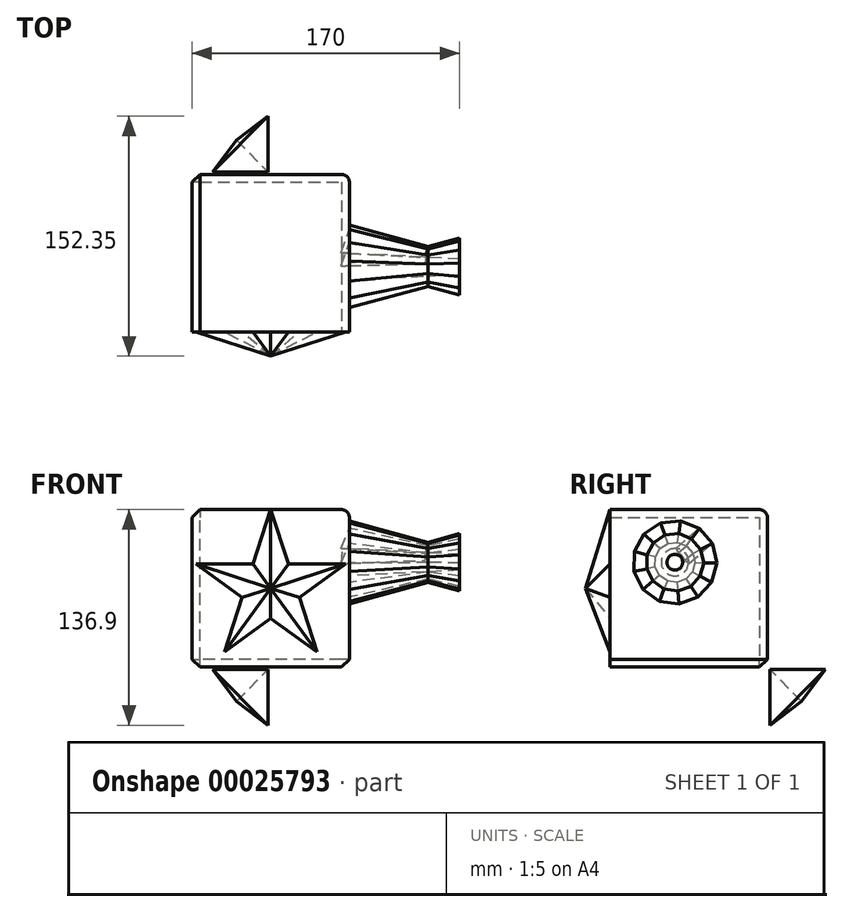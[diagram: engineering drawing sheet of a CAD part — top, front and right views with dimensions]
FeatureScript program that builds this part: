
annotation { "Feature Type Name" : "Feature", "Feature Type Description" : "" }
export const myFeature = defineFeature(function(context is Context, id is Id, definition is map)
    precondition{}
    {
        {
            var Q0;
            Q0=qCreatedBy(makeId("Top.planeOp"),FACE);
            var sketch = newSketch(context, id + "F0", { "sketchPlane" : qUnion([Q0])});
            skLineSegment(sketch, "E0.rect.bottom", {"start": v(50, -50) * mm, "end": v(-50, -50) * mm});
            skLineSegment(sketch, "E0.rect.top", {"start": v(50, 50) * mm, "end": v(-50, 50) * mm});
            skLineSegment(sketch, "E0.rect.left", {"start": v(50, -50) * mm, "end": v(50, 50) * mm});
            skLineSegment(sketch, "E0.rect.right", {"start": v(-50, -50) * mm, "end": v(-50, 50) * mm});
            skPoint(sketch, "E0.rect.middle", {"position": v(0, 0) * mm});
            skSolve(sketch);
        }
        {
            var Q0;
            Q0=makeQuery(id+"F0.imprint","IMPRINT",FACE,{"disambiguationData":[TD([[makeQuery(id+"F0.imprint","IMPRINT",EDGE,{"derivedFrom":sQuery(id+"F0.wireOp",EDGE,"E0.rect.bottom")}),-1.0]])]});
            extrude(context, id + "F1", {"entities" : qUnion([Q0]), "depth" : 100 * mm});
        }
        {
            var Q0;
            Q0=makeQuery(id+"F1.opExtrude","SWEPT_FACE",FACE,{"disambiguationData":[OSD([sQuery(id+"F0.wireOp",EDGE,"E0.rect.left")])]});
            var sketch = newSketch(context, id + "F2", { "sketchPlane" : qUnion([Q0])});
            skCircle(sketch, "E1.cCircle", {"center": v(-8.75, 66.58) * mm, "radius": 25.84 * mm, "construction": true});
            skLineSegment(sketch, "E1.0", {"start": v(17.86, 66.11) * mm, "end": v(14.6, 53.8) * mm});
            skLineSegment(sketch, "E1.1", {"start": v(14.6, 53.8) * mm, "end": v(5.98, 44.41) * mm});
            skLineSegment(sketch, "E1.2", {"start": v(5.98, 44.41) * mm, "end": v(-6, 40.1) * mm});
            skLineSegment(sketch, "E1.3", {"start": v(-6, 40.1) * mm, "end": v(-18.62, 41.86) * mm});
            skLineSegment(sketch, "E1.4", {"start": v(-18.62, 41.86) * mm, "end": v(-28.98, 49.28) * mm});
            skLineSegment(sketch, "E1.5", {"start": v(-28.98, 49.28) * mm, "end": v(-34.7, 60.66) * mm});
            skLineSegment(sketch, "E1.6", {"start": v(-34.7, 60.66) * mm, "end": v(-34.48, 73.4) * mm});
            skLineSegment(sketch, "E1.7", {"start": v(-34.48, 73.4) * mm, "end": v(-28.37, 84.57) * mm});
            skLineSegment(sketch, "E1.8", {"start": v(-28.37, 84.57) * mm, "end": v(-17.76, 91.62) * mm});
            skLineSegment(sketch, "E1.9", {"start": v(-17.76, 91.62) * mm, "end": v(-5.09, 92.94) * mm});
            skLineSegment(sketch, "E1.10", {"start": v(-5.09, 92.94) * mm, "end": v(6.74, 88.21) * mm});
            skLineSegment(sketch, "E1.11", {"start": v(6.74, 88.21) * mm, "end": v(15.02, 78.53) * mm});
            skLineSegment(sketch, "E1.12", {"start": v(15.02, 78.53) * mm, "end": v(17.86, 66.11) * mm});
            skPoint(sketch, "E1.0.midPoint", {"position": v(16.23, 59.96) * mm});
            skSolve(sketch);
        }
        {
            var Q0;
            Q0=makeQuery(id+"F2.imprint","IMPRINT",FACE,{"disambiguationData":[TD([[makeQuery(id+"F2.imprint","IMPRINT",EDGE,{"derivedFrom":sQuery(id+"F2.wireOp",EDGE,"E1.0")}),-1.0]])]});
            extrude(context, id + "F3", {"entities" : qUnion([Q0]), "operationType" : NewBodyOperationType.ADD, "depth" : 50 * mm, "hasDraft" : true, "draftAngle" : 15 * degree, "draftPullDirection" : true});
        }
        {
            var Q0;
            Q0=makeQuery(id+"F3.opExtrude","CAP_FACE",FACE,{"disambiguationData":[OSD([sQuery(id+"F2.wireOp",EDGE,"E1.0"),sQuery(id+"F2.wireOp",EDGE,"E1.1"),sQuery(id+"F2.wireOp",EDGE,"E1.2"),sQuery(id+"F2.wireOp",EDGE,"E1.3"),sQuery(id+"F2.wireOp",EDGE,"E1.4"),sQuery(id+"F2.wireOp",EDGE,"E1.5"),sQuery(id+"F2.wireOp",EDGE,"E1.6"),sQuery(id+"F2.wireOp",EDGE,"E1.7"),sQuery(id+"F2.wireOp",EDGE,"E1.8"),sQuery(id+"F2.wireOp",EDGE,"E1.9"),sQuery(id+"F2.wireOp",EDGE,"E1.10"),sQuery(id+"F2.wireOp",EDGE,"E1.11"),sQuery(id+"F2.wireOp",EDGE,"E1.12")])],"isStart":false});
            var sketch = newSketch(context, id + "F4", { "sketchPlane" : qUnion([Q0])});
            skLineSegment(sketch, "E2", {"start": v(-6.99, 79.27) * mm, "end": v(-1.3, 77) * mm});
            skLineSegment(sketch, "E3", {"start": v(-1.3, 77) * mm, "end": v(2.7, 72.33) * mm});
            skLineSegment(sketch, "E4", {"start": v(2.7, 72.33) * mm, "end": v(4.06, 66.35) * mm});
            skLineSegment(sketch, "E5", {"start": v(4.06, 66.35) * mm, "end": v(2.49, 60.42) * mm});
            skLineSegment(sketch, "E6", {"start": v(2.49, 60.42) * mm, "end": v(-1.66, 55.9) * mm});
            skLineSegment(sketch, "E7", {"start": v(-1.66, 55.9) * mm, "end": v(-7.43, 53.83) * mm});
            skLineSegment(sketch, "E8", {"start": v(-7.43, 53.83) * mm, "end": v(-13.5, 54.67) * mm});
            skLineSegment(sketch, "E9", {"start": v(-13.5, 54.67) * mm, "end": v(-18.5, 58.25) * mm});
            skLineSegment(sketch, "E10", {"start": v(-18.5, 58.25) * mm, "end": v(-21.25, 63.73) * mm});
            skLineSegment(sketch, "E11", {"start": v(-21.25, 63.73) * mm, "end": v(-21.14, 69.86) * mm});
            skLineSegment(sketch, "E12", {"start": v(-21.14, 69.86) * mm, "end": v(-18.2, 75.24) * mm});
            skLineSegment(sketch, "E13", {"start": v(-18.2, 75.24) * mm, "end": v(-13.1, 78.64) * mm});
            skLineSegment(sketch, "E14", {"start": v(-13.1, 78.64) * mm, "end": v(-6.99, 79.27) * mm});
            skSolve(sketch);
        }
        {
            var Q0;
            Q0 = qSketchRegion(id + "F4", true);
            extrude(context, id + "F5", {"entities" : qUnion([Q0]), "operationType" : NewBodyOperationType.ADD, "depth" : 20 * mm, "hasDraft" : true, "draftAngle" : 15 * degree});
        }
        {
            var Q0;
            Q0=makeQuery(id+"F5.opExtrude","CAP_FACE",FACE,{"disambiguationData":[OSD([sQuery(id+"F4.wireOp",EDGE,"E2"),sQuery(id+"F4.wireOp",EDGE,"E3"),sQuery(id+"F4.wireOp",EDGE,"E4"),sQuery(id+"F4.wireOp",EDGE,"E5"),sQuery(id+"F4.wireOp",EDGE,"E6"),sQuery(id+"F4.wireOp",EDGE,"E7"),sQuery(id+"F4.wireOp",EDGE,"E8"),sQuery(id+"F4.wireOp",EDGE,"E9"),sQuery(id+"F4.wireOp",EDGE,"E10"),sQuery(id+"F4.wireOp",EDGE,"E11"),sQuery(id+"F4.wireOp",EDGE,"E12"),sQuery(id+"F4.wireOp",EDGE,"E13"),sQuery(id+"F4.wireOp",EDGE,"E14")])],"isStart":false});
            var sketch = newSketch(context, id + "F6", { "sketchPlane" : qUnion([Q0])});
            skLineSegment(sketch, "E15", {"start": v(-26.63, 62.5) * mm, "end": v(8.6, 70.54) * mm});
            skLineSegment(sketch, "E16", {"start": v(8.6, 70.54) * mm, "end": v(-14.96, 83.83) * mm});
            skLineSegment(sketch, "E17", {"start": v(-14.96, 83.83) * mm, "end": v(-2.73, 49.82) * mm});
            skLineSegment(sketch, "E18", {"start": v(-2.73, 49.82) * mm, "end": v(-26.48, 71.27) * mm});
            skLineSegment(sketch, "E19", {"start": v(-26.48, 71.27) * mm, "end": v(8.46, 62.02) * mm});
            skCircle(sketch, "E20", {"center": v(-8.75, 66.58) * mm, "radius": 5 * mm});
            skSolve(sketch);
        }
        {
            var Q0;
            {var subQ1=sQuery(id+"F6.wireOp",EDGE,"E15");var subQ3=sQuery(id+"F6.wireOp",EDGE,"E20");var subQ5=makeQuery(id+"F6.imprint","INTERSECT",VERTEX,{"disambiguationData":[OD(0.0)],"derivedFrom":[subQ1,subQ3]});Q0=makeQuery(id+"F6.imprint","IMPRINT",FACE,{"disambiguationData":[TD([[makeQuery(id+"F6.imprint","IMPRINT",EDGE,{"disambiguationData":[TD([[subQ5,-1.0]])],"derivedFrom":subQ3}),1.0]])]});}
            var Q1;
            {var subQ0=sQuery(id+"F6.wireOp",EDGE,"E20");var subQ3=sQuery(id+"F6.wireOp",EDGE,"E15");var subQ4=makeQuery(id+"F6.imprint","INTERSECT",VERTEX,{"disambiguationData":[OD(0.0)],"derivedFrom":[subQ3,subQ0]});Q1=makeQuery(id+"F6.imprint","IMPRINT",FACE,{"disambiguationData":[TD([[makeQuery(id+"F6.imprint","IMPRINT",EDGE,{"disambiguationData":[TD([[subQ4,1.0]])],"derivedFrom":subQ0}),1.0]])]});}
            var Q2;
            {var subQ0=sQuery(id+"F6.wireOp",EDGE,"E20");var subQ3=sQuery(id+"F6.wireOp",EDGE,"E17");var subQ4=makeQuery(id+"F6.imprint","INTERSECT",VERTEX,{"disambiguationData":[OD(0.0)],"derivedFrom":[subQ3,subQ0]});Q2=makeQuery(id+"F6.imprint","IMPRINT",FACE,{"disambiguationData":[TD([[makeQuery(id+"F6.imprint","IMPRINT",EDGE,{"disambiguationData":[TD([[subQ4,-1.0]])],"derivedFrom":subQ0}),1.0]])]});}
            var Q3;
            {var subQ0=sQuery(id+"F6.wireOp",EDGE,"E20");var subQ3=sQuery(id+"F6.wireOp",EDGE,"E15");var subQ4=makeQuery(id+"F6.imprint","INTERSECT",VERTEX,{"disambiguationData":[OD(1.0)],"derivedFrom":[subQ3,subQ0]});Q3=makeQuery(id+"F6.imprint","IMPRINT",FACE,{"disambiguationData":[TD([[makeQuery(id+"F6.imprint","IMPRINT",EDGE,{"disambiguationData":[TD([[subQ4,-1.0]])],"derivedFrom":subQ0}),1.0]])]});}
            var Q4;
            {var subQ0=sQuery(id+"F6.wireOp",EDGE,"E20");var subQ3=sQuery(id+"F6.wireOp",EDGE,"E15");var subQ4=makeQuery(id+"F6.imprint","INTERSECT",VERTEX,{"disambiguationData":[OD(1.0)],"derivedFrom":[subQ3,subQ0]});Q4=makeQuery(id+"F6.imprint","IMPRINT",FACE,{"disambiguationData":[TD([[makeQuery(id+"F6.imprint","IMPRINT",EDGE,{"disambiguationData":[TD([[subQ4,1.0]])],"derivedFrom":subQ0}),1.0]])]});}
            var Q5;
            {var subQ0=sQuery(id+"F6.wireOp",EDGE,"E20");var subQ3=sQuery(id+"F6.wireOp",EDGE,"E17");var subQ4=makeQuery(id+"F6.imprint","INTERSECT",VERTEX,{"disambiguationData":[OD(1.0)],"derivedFrom":[subQ3,subQ0]});Q5=makeQuery(id+"F6.imprint","IMPRINT",FACE,{"disambiguationData":[TD([[makeQuery(id+"F6.imprint","IMPRINT",EDGE,{"disambiguationData":[TD([[subQ4,-1.0]])],"derivedFrom":subQ0}),1.0]])]});}
            var Q6;
            Q6=makeQuery(id+"F1.opExtrude","SWEPT_FACE",FACE,{"disambiguationData":[OSD([sQuery(id+"F0.wireOp",EDGE,"E0.rect.left")])]});
            extrude(context, id + "F7", {"entities" : qUnion([Q0, Q1, Q2, Q3, Q4, Q5]), "operationType" : NewBodyOperationType.REMOVE, "endBound" : BoundingType.UP_TO_SURFACE, "oppositeDirection" : true, "endBoundEntityFace" : qUnion([Q6]), "depth" : 70 * mm, "hasDraft" : true, "draftAngle" : 3 * degree});
        }
        {
            var Q0;
            Q0=makeQuery(id+"F3.opExtrude","SWEPT_FACE",FACE,{"disambiguationData":[OSD([sQuery(id+"F2.wireOp",EDGE,"E1.11")])]});
            var sketch = newSketch(context, id + "F8", { "sketchPlane" : qUnion([Q0])});
            skLineSegment(sketch, "E21", {"start": v(-32.13, 62.65) * mm, "end": v(-32.13, 49.92) * mm});
            skLineSegment(sketch, "E22", {"start": v(-32.13, 49.92) * mm, "end": v(-83.9, 53.22) * mm});
            skLineSegment(sketch, "E23", {"start": v(-83.9, 53.22) * mm, "end": v(-83.9, 59.35) * mm});
            skLineSegment(sketch, "E24", {"start": v(-83.9, 59.35) * mm, "end": v(-32.13, 62.65) * mm});
            skSolve(sketch);
        }
        {
            var Q0;
            Q0 = qSketchRegion(id + "F8", true);
            var Q1;
            Q1=makeQuery(id+"F7.boolean.opBoolean","COPY",FACE,{"derivedFrom":makeQuery(id+"F7.opExtrude","SWEPT_FACE",FACE,{"disambiguationData":[OSD([sQuery(id+"F6.wireOp",EDGE,"E20")])]})});
            extrude(context, id + "F9", {"entities" : qUnion([Q0]), "operationType" : NewBodyOperationType.REMOVE, "endBound" : BoundingType.UP_TO_SURFACE, "oppositeDirection" : true, "endBoundEntityFace" : qUnion([Q1]), "depth" : 25 * mm});
        }
        {
            var Q0;
            Q0=makeQuery(id+"F1.opExtrude","CAP_EDGE",EDGE,{"disambiguationData":[OSD([sQuery(id+"F0.wireOp",EDGE,"E0.rect.top")])],"isStart":false});
            var Q1;
            Q1=makeQuery(id+"F1.opExtrude","CAP_EDGE",EDGE,{"disambiguationData":[OSD([sQuery(id+"F0.wireOp",EDGE,"E0.rect.left")])],"isStart":false});
            var Q2;
            Q2=makeQuery(id+"F1.opExtrude","SWEPT_EDGE",EDGE,{"disambiguationData":[OSD([sQuery(id+"F0.wireOp",EDGE,"E0.rect.top"),sQuery(id+"F0.wireOp",EDGE,"E0.rect.left")])]});
            fillet(context, id + "F10", {"entities" : qUnion([Q0, Q1, Q2]), "radius" : 5 * mm, "tangentPropagation" : true, "allowEdgeOverflow" : false});
        }
        {
            var Q0;
            Q0=makeQuery(id+"F1.opExtrude","SWEPT_EDGE",EDGE,{"disambiguationData":[OSD([sQuery(id+"F0.wireOp",EDGE,"E0.rect.top"),sQuery(id+"F0.wireOp",EDGE,"E0.rect.right")])]});
            var Q1;
            Q1=makeQuery(id+"F1.opExtrude","CAP_EDGE",EDGE,{"disambiguationData":[OSD([sQuery(id+"F0.wireOp",EDGE,"E0.rect.top")])],"isStart":true});
            var Q2;
            Q2=makeQuery(id+"F1.opExtrude","CAP_EDGE",EDGE,{"disambiguationData":[OSD([sQuery(id+"F0.wireOp",EDGE,"E0.rect.right")])],"isStart":true});
            chamfer(context, id + "F11", {"entities" : qUnion([Q0, Q1, Q2]), "width" : 5 * mm, "tangentPropagation" : true});
        }
        {
            var Q0;
            {var subQ0=sQuery(id+"F0.wireOp",EDGE,"E0.rect.top");var subQ1=sQuery(id+"F0.wireOp",EDGE,"E0.rect.right");Q0=makeQuery(id+"F11.opChamfer","BLEND_FACE",FACE,{"disambiguationData":[OSD([subQ0,subQ1]),TDD([makeQuery(id+"F1.opExtrude","CAP_VERTEX",VERTEX,{"disambiguationData":[OSD([subQ0,subQ1])],"isStart":true})])]});}
            var sketch = newSketch(context, id + "F12", { "sketchPlane" : qUnion([Q0])});
            skLineSegment(sketch, "E25", {"start": v(-34.85, 10.36) * mm, "end": v(8.46, 35.36) * mm});
            skLineSegment(sketch, "E26", {"start": v(8.46, 35.36) * mm, "end": v(-34.85, 60.36) * mm});
            skLineSegment(sketch, "E27", {"start": v(-34.85, 60.36) * mm, "end": v(-34.85, 10.36) * mm});
            skLineSegment(sketch, "E28", {"start": v(-34.85, 60.36) * mm, "end": v(-13.2, 22.86) * mm});
            skLineSegment(sketch, "E29", {"start": v(-34.85, 10.36) * mm, "end": v(-13.2, 47.86) * mm});
            skLineSegment(sketch, "E30", {"start": v(8.46, 35.36) * mm, "end": v(-34.85, 35.36) * mm});
            skSolve(sketch);
        }
        {
            var Q0;
            Q0 = qSketchRegion(id + "F12", true);
            extrude(context, id + "F13", {"entities" : qUnion([Q0]), "operationType" : NewBodyOperationType.ADD, "depth" : 25 * mm, "hasDraft" : true, "draftAngle" : 45 * degree, "draftPullDirection" : true});
        }
        {
            var Q0;
            Q0=makeQuery(id+"F1.opExtrude","SWEPT_FACE",FACE,{"disambiguationData":[OSD([sQuery(id+"F0.wireOp",EDGE,"E0.rect.bottom")])]});
            var sketch = newSketch(context, id + "F14", { "sketchPlane" : qUnion([Q0])});
            skLineSegment(sketch, "E31", {"start": v(47.5, 2.5) * mm, "end": v(-47.5, 97.5) * mm});
            skLineSegment(sketch, "E32", {"start": v(-47.5, 97.5) * mm, "end": v(-47.5, 2.5) * mm});
            skLineSegment(sketch, "E33", {"start": v(-47.5, 2.5) * mm, "end": v(48.54, 98.54) * mm});
            skLineSegment(sketch, "E34", {"start": v(0, 50) * mm, "end": v(0, 100) * mm});
            skLineSegment(sketch, "E35", {"start": v(0, 50) * mm, "end": v(-47.55, 65.45) * mm});
            skLineSegment(sketch, "E36", {"start": v(0, 50) * mm, "end": v(47.55, 65.45) * mm});
            skLineSegment(sketch, "E37", {"start": v(0, 50) * mm, "end": v(-29.39, 9.55) * mm});
            skLineSegment(sketch, "E38", {"start": v(0, 50) * mm, "end": v(29.39, 9.55) * mm});
            skLineSegment(sketch, "E39", {"start": v(-47.55, 65.45) * mm, "end": v(47.55, 65.45) * mm});
            skLineSegment(sketch, "E40", {"start": v(47.55, 65.45) * mm, "end": v(-29.39, 9.55) * mm});
            skLineSegment(sketch, "E41", {"start": v(-29.39, 9.55) * mm, "end": v(0, 100) * mm});
            skLineSegment(sketch, "E42", {"start": v(0, 100) * mm, "end": v(29.39, 9.55) * mm});
            skLineSegment(sketch, "E43", {"start": v(29.39, 9.55) * mm, "end": v(-47.55, 65.45) * mm});
            skSolve(sketch);
        }
        {
            var Q0;
            {var subQ0=sQuery(id+"F14.wireOp",EDGE,"E42");var subQ3=sQuery(id+"F14.wireOp",EDGE,"E31");var subQ4=makeQuery(id+"F14.imprint","INTERSECT",VERTEX,{"derivedFrom":[subQ3,subQ0]});Q0=makeQuery(id+"F14.imprint","IMPRINT",FACE,{"disambiguationData":[TD([[makeQuery(id+"F14.imprint","IMPRINT",EDGE,{"disambiguationData":[TD([[subQ4,-1.0]])],"derivedFrom":subQ3}),-1.0]])]});}
            var Q1;
            {var subQ0=sQuery(id+"F14.wireOp",EDGE,"E41");var subQ3=sQuery(id+"F14.wireOp",EDGE,"E31");var subQ4=makeQuery(id+"F14.imprint","INTERSECT",VERTEX,{"derivedFrom":[subQ3,subQ0]});Q1=makeQuery(id+"F14.imprint","IMPRINT",FACE,{"disambiguationData":[TD([[makeQuery(id+"F14.imprint","IMPRINT",EDGE,{"disambiguationData":[TD([[subQ4,-1.0]])],"derivedFrom":subQ3}),-1.0]])]});}
            var Q2;
            {var subQ0=sQuery(id+"F14.wireOp",EDGE,"E39");var subQ1=sQuery(id+"F14.wireOp",EDGE,"E32");var subQ2=makeQuery(id+"F14.imprint","INTERSECT",VERTEX,{"derivedFrom":[subQ1,subQ0]});Q2=makeQuery(id+"F14.imprint","IMPRINT",FACE,{"disambiguationData":[TD([[makeQuery(id+"F14.imprint","IMPRINT",EDGE,{"disambiguationData":[TD([[subQ2,-1.0]])],"derivedFrom":subQ1}),-1.0]])]});}
            var Q3;
            {var subQ1=sQuery(id+"F14.wireOp",EDGE,"E32");var subQ3=sQuery(id+"F14.wireOp",EDGE,"E35");var subQ5=makeQuery(id+"F14.imprint","INTERSECT",VERTEX,{"derivedFrom":[subQ1,subQ3]});Q3=makeQuery(id+"F14.imprint","IMPRINT",FACE,{"disambiguationData":[TD([[makeQuery(id+"F14.imprint","IMPRINT",EDGE,{"disambiguationData":[TD([[subQ5,-1.0]])],"derivedFrom":subQ1}),-1.0]])]});}
            var Q4;
            {var subQ0=sQuery(id+"F14.wireOp",EDGE,"E42");var subQ3=sQuery(id+"F14.wireOp",EDGE,"E33");var subQ4=makeQuery(id+"F14.imprint","INTERSECT",VERTEX,{"derivedFrom":[subQ3,subQ0]});Q4=makeQuery(id+"F14.imprint","IMPRINT",FACE,{"disambiguationData":[TD([[makeQuery(id+"F14.imprint","IMPRINT",EDGE,{"disambiguationData":[TD([[subQ4,-1.0]])],"derivedFrom":subQ3}),1.0]])]});}
            var Q5;
            {var subQ0=sQuery(id+"F14.wireOp",EDGE,"E42");var subQ3=sQuery(id+"F14.wireOp",EDGE,"E36");var subQ4=makeQuery(id+"F14.imprint","INTERSECT",VERTEX,{"derivedFrom":[subQ3,subQ0]});Q5=makeQuery(id+"F14.imprint","IMPRINT",FACE,{"disambiguationData":[TD([[makeQuery(id+"F14.imprint","IMPRINT",EDGE,{"disambiguationData":[TD([[subQ4,-1.0]])],"derivedFrom":subQ0}),1.0]])]});}
            var Q6;
            {var subQ0=sQuery(id+"F14.wireOp",EDGE,"E43");var subQ3=sQuery(id+"F14.wireOp",EDGE,"E37");var subQ4=makeQuery(id+"F14.imprint","INTERSECT",VERTEX,{"derivedFrom":[subQ3,subQ0]});Q6=makeQuery(id+"F14.imprint","IMPRINT",FACE,{"disambiguationData":[TD([[makeQuery(id+"F14.imprint","IMPRINT",EDGE,{"disambiguationData":[TD([[subQ4,1.0]])],"derivedFrom":subQ0}),1.0]])]});}
            var Q7;
            {var subQ1=sQuery(id+"F14.wireOp",EDGE,"E40");var subQ3=sQuery(id+"F14.wireOp",EDGE,"E38");var subQ5=makeQuery(id+"F14.imprint","INTERSECT",VERTEX,{"derivedFrom":[subQ3,subQ1]});Q7=makeQuery(id+"F14.imprint","IMPRINT",FACE,{"disambiguationData":[TD([[makeQuery(id+"F14.imprint","IMPRINT",EDGE,{"disambiguationData":[TD([[subQ5,-1.0]])],"derivedFrom":subQ1}),1.0]])]});}
            var Q8;
            {var subQ0=sQuery(id+"F14.wireOp",EDGE,"E42");var subQ1=sQuery(id+"F14.wireOp",EDGE,"E31");var subQ2=makeQuery(id+"F14.imprint","INTERSECT",VERTEX,{"derivedFrom":[subQ1,subQ0]});Q8=makeQuery(id+"F14.imprint","IMPRINT",FACE,{"disambiguationData":[TD([[makeQuery(id+"F14.imprint","IMPRINT",EDGE,{"disambiguationData":[TD([[subQ2,-1.0]])],"derivedFrom":subQ1}),1.0]])]});}
            var Q9;
            {var subQ1=sQuery(id+"F14.wireOp",EDGE,"E40");var subQ5=sQuery(id+"F14.wireOp",EDGE,"E31");var subQ6=makeQuery(id+"F14.imprint","INTERSECT",VERTEX,{"derivedFrom":[subQ5,subQ1]});Q9=makeQuery(id+"F14.imprint","IMPRINT",FACE,{"disambiguationData":[TD([[makeQuery(id+"F14.imprint","IMPRINT",EDGE,{"disambiguationData":[TD([[subQ6,1.0]])],"derivedFrom":subQ1}),-1.0]])]});}
            var Q10;
            {var subQ3=sQuery(id+"F14.wireOp",EDGE,"E33");var subQ5=sQuery(id+"F14.wireOp",EDGE,"E41");var subQ6=makeQuery(id+"F14.imprint","INTERSECT",VERTEX,{"derivedFrom":[subQ3,subQ5]});Q10=makeQuery(id+"F14.imprint","IMPRINT",FACE,{"disambiguationData":[TD([[makeQuery(id+"F14.imprint","IMPRINT",EDGE,{"disambiguationData":[TD([[subQ6,-1.0]])],"derivedFrom":subQ3}),-1.0]])]});}
            var Q11;
            {var subQ0=sQuery(id+"F14.wireOp",EDGE,"E42");var subQ3=sQuery(id+"F14.wireOp",EDGE,"E33");var subQ4=makeQuery(id+"F14.imprint","INTERSECT",VERTEX,{"derivedFrom":[subQ3,subQ0]});Q11=makeQuery(id+"F14.imprint","IMPRINT",FACE,{"disambiguationData":[TD([[makeQuery(id+"F14.imprint","IMPRINT",EDGE,{"disambiguationData":[TD([[subQ4,-1.0]])],"derivedFrom":subQ3}),-1.0]])]});}
            var Q12;
            {var subQ0=sQuery(id+"F14.wireOp",EDGE,"E41");var subQ3=sQuery(id+"F14.wireOp",EDGE,"E31");var subQ4=makeQuery(id+"F14.imprint","INTERSECT",VERTEX,{"derivedFrom":[subQ3,subQ0]});Q12=makeQuery(id+"F14.imprint","IMPRINT",FACE,{"disambiguationData":[TD([[makeQuery(id+"F14.imprint","IMPRINT",EDGE,{"disambiguationData":[TD([[subQ4,1.0]])],"derivedFrom":subQ0}),-1.0]])]});}
            var Q13;
            {var subQ0=sQuery(id+"F14.wireOp",EDGE,"E41");var subQ3=sQuery(id+"F14.wireOp",EDGE,"E31");var subQ4=makeQuery(id+"F14.imprint","INTERSECT",VERTEX,{"derivedFrom":[subQ3,subQ0]});Q13=makeQuery(id+"F14.imprint","IMPRINT",FACE,{"disambiguationData":[TD([[makeQuery(id+"F14.imprint","IMPRINT",EDGE,{"disambiguationData":[TD([[subQ4,-1.0]])],"derivedFrom":subQ3}),1.0]])]});}
            var Q14;
            {var subQ3=sQuery(id+"F14.wireOp",EDGE,"E32");var subQ5=sQuery(id+"F14.wireOp",EDGE,"E35");var subQ7=makeQuery(id+"F14.imprint","INTERSECT",VERTEX,{"derivedFrom":[subQ3,subQ5]});Q14=makeQuery(id+"F14.imprint","IMPRINT",FACE,{"disambiguationData":[TD([[makeQuery(id+"F14.imprint","IMPRINT",EDGE,{"disambiguationData":[TD([[subQ7,-1.0]])],"derivedFrom":subQ3}),1.0]])]});}
            var Q15;
            {var subQ1=sQuery(id+"F14.wireOp",EDGE,"E41");var subQ5=sQuery(id+"F14.wireOp",EDGE,"E35");var subQ6=makeQuery(id+"F14.imprint","INTERSECT",VERTEX,{"derivedFrom":[subQ5,subQ1]});Q15=makeQuery(id+"F14.imprint","IMPRINT",FACE,{"disambiguationData":[TD([[makeQuery(id+"F14.imprint","IMPRINT",EDGE,{"disambiguationData":[TD([[subQ6,1.0]])],"derivedFrom":subQ1}),-1.0]])]});}
            var Q16;
            {var subQ1=sQuery(id+"F14.wireOp",EDGE,"E41");var subQ3=sQuery(id+"F14.wireOp",EDGE,"E33");var subQ5=makeQuery(id+"F14.imprint","INTERSECT",VERTEX,{"derivedFrom":[subQ3,subQ1]});Q16=makeQuery(id+"F14.imprint","IMPRINT",FACE,{"disambiguationData":[TD([[makeQuery(id+"F14.imprint","IMPRINT",EDGE,{"disambiguationData":[TD([[subQ5,-1.0]])],"derivedFrom":subQ3}),1.0]])]});}
            var Q17;
            {var subQ1=sQuery(id+"F14.wireOp",EDGE,"E39");var subQ3=sQuery(id+"F14.wireOp",EDGE,"E34");var subQ5=makeQuery(id+"F14.imprint","INTERSECT",VERTEX,{"derivedFrom":[subQ3,subQ1]});Q17=makeQuery(id+"F14.imprint","IMPRINT",FACE,{"disambiguationData":[TD([[makeQuery(id+"F14.imprint","IMPRINT",EDGE,{"disambiguationData":[TD([[subQ5,1.0]])],"derivedFrom":subQ1}),1.0]])]});}
            var Q18;
            {var subQ1=sQuery(id+"F14.wireOp",EDGE,"E39");var subQ3=sQuery(id+"F14.wireOp",EDGE,"E34");var subQ5=makeQuery(id+"F14.imprint","INTERSECT",VERTEX,{"derivedFrom":[subQ3,subQ1]});Q18=makeQuery(id+"F14.imprint","IMPRINT",FACE,{"disambiguationData":[TD([[makeQuery(id+"F14.imprint","IMPRINT",EDGE,{"disambiguationData":[TD([[subQ5,-1.0]])],"derivedFrom":subQ1}),1.0]])]});}
            var Q19;
            {var subQ1=sQuery(id+"F14.wireOp",EDGE,"E39");var subQ5=sQuery(id+"F14.wireOp",EDGE,"E34");var subQ6=makeQuery(id+"F14.imprint","INTERSECT",VERTEX,{"derivedFrom":[subQ5,subQ1]});Q19=makeQuery(id+"F14.imprint","IMPRINT",FACE,{"disambiguationData":[TD([[makeQuery(id+"F14.imprint","IMPRINT",EDGE,{"disambiguationData":[TD([[subQ6,-1.0]])],"derivedFrom":subQ1}),-1.0]])]});}
            var Q20;
            {var subQ1=sQuery(id+"F14.wireOp",EDGE,"E39");var subQ5=sQuery(id+"F14.wireOp",EDGE,"E34");var subQ6=makeQuery(id+"F14.imprint","INTERSECT",VERTEX,{"derivedFrom":[subQ5,subQ1]});Q20=makeQuery(id+"F14.imprint","IMPRINT",FACE,{"disambiguationData":[TD([[makeQuery(id+"F14.imprint","IMPRINT",EDGE,{"disambiguationData":[TD([[subQ6,1.0]])],"derivedFrom":subQ1}),-1.0]])]});}
            var Q21;
            {var subQ1=sQuery(id+"F14.wireOp",EDGE,"E40");var subQ5=sQuery(id+"F14.wireOp",EDGE,"E38");var subQ6=makeQuery(id+"F14.imprint","INTERSECT",VERTEX,{"derivedFrom":[subQ5,subQ1]});Q21=makeQuery(id+"F14.imprint","IMPRINT",FACE,{"disambiguationData":[TD([[makeQuery(id+"F14.imprint","IMPRINT",EDGE,{"disambiguationData":[TD([[subQ6,-1.0]])],"derivedFrom":subQ1}),-1.0]])]});}
            var Q22;
            {var subQ0=sQuery(id+"F14.wireOp",EDGE,"E43");var subQ3=sQuery(id+"F14.wireOp",EDGE,"E33");var subQ4=makeQuery(id+"F14.imprint","INTERSECT",VERTEX,{"derivedFrom":[subQ3,subQ0]});Q22=makeQuery(id+"F14.imprint","IMPRINT",FACE,{"disambiguationData":[TD([[makeQuery(id+"F14.imprint","IMPRINT",EDGE,{"disambiguationData":[TD([[subQ4,1.0]])],"derivedFrom":subQ0}),-1.0]])]});}
            var Q23;
            {var subQ0=sQuery(id+"F14.wireOp",EDGE,"E40");var subQ3=sQuery(id+"F14.wireOp",EDGE,"E31");var subQ4=makeQuery(id+"F14.imprint","INTERSECT",VERTEX,{"derivedFrom":[subQ3,subQ0]});Q23=makeQuery(id+"F14.imprint","IMPRINT",FACE,{"disambiguationData":[TD([[makeQuery(id+"F14.imprint","IMPRINT",EDGE,{"disambiguationData":[TD([[subQ4,-1.0]])],"derivedFrom":subQ0}),-1.0]])]});}
            var Q24;
            {var subQ0=sQuery(id+"F14.wireOp",EDGE,"E42");var subQ3=sQuery(id+"F14.wireOp",EDGE,"E33");var subQ4=makeQuery(id+"F14.imprint","INTERSECT",VERTEX,{"derivedFrom":[subQ3,subQ0]});Q24=makeQuery(id+"F14.imprint","IMPRINT",FACE,{"disambiguationData":[TD([[makeQuery(id+"F14.imprint","IMPRINT",EDGE,{"disambiguationData":[TD([[subQ4,-1.0]])],"derivedFrom":subQ0}),-1.0]])]});}
            extrude(context, id + "F15", {"entities" : qUnion([Q0, Q1, Q2, Q3, Q4, Q5, Q6, Q7, Q8, Q9, Q10, Q11, Q12, Q13, Q14, Q15, Q16, Q17, Q18, Q19, Q20, Q21, Q22, Q23, Q24]), "operationType" : NewBodyOperationType.ADD, "depth" : 25 * mm, "hasDraft" : true, "draftAngle" : 45 * degree, "draftPullDirection" : true});
        }
    });
